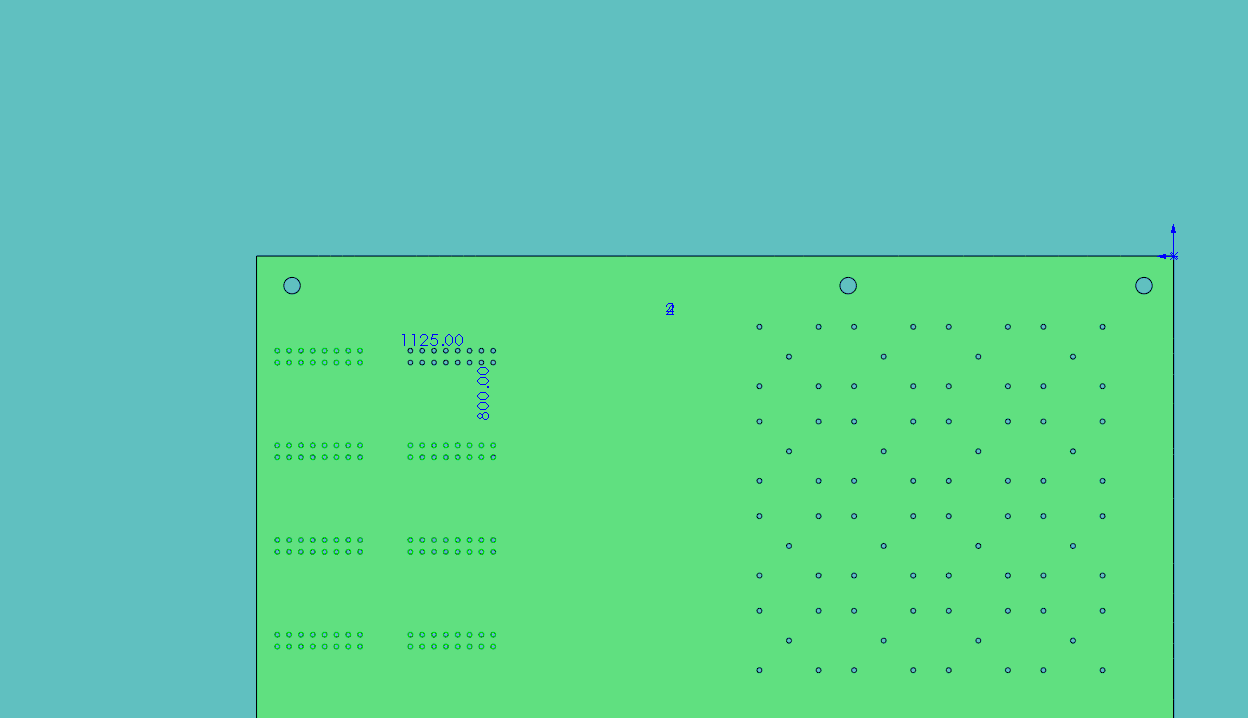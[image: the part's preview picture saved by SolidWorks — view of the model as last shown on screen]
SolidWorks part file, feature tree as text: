
SOLIDWORKS PART (.sldprt)
format: sldprt  version: not decoded by parser v0  size: 470,016 bytes
history: native  units: mm
features: sketch x4, cut_extrude x3, pattern_linear x2, material x1, extrude x1 (+13 scaffold rows collapsed)
feature tree (24):
  scaffold x13  (default folders/planes/origin — collapsed)
  material  "Material <not specified>"
  sketch  "Sketch1"  dims[D1=196.85mm D2=114.3mm]
  extrude  "PCB outline"  Depth=1.5748mm
  sketch  "mounting holes"  dims[c1.D1=3.556mm c1.D4=3.556mm c1.D7=3.556mm c1.D8=3.556mm c2.D4=3.556mm c2.D5=3.556mm c2.D6=3.556mm c2.D7=3.556mm c2.D8=3.556mm c2.D12=3.556mm c2.D13=3.556mm c2.D2=6.35mm c2.D3=6.35mm c3.D5=6.35mm c3.D6=6.35mm c3.D9=83.82mm c3.D10=~189.648312mm c3.D11=~7.201688mm c4.D10=6.35mm c4.D11=190.5mm c4.D9=96.52mm c5.D10=63.5mm c5.D11=119.38mm c5.D14=25.4mm]
  cut_extrude  "mounting holes cut"  Depth=2.54mm
  sketch  "Sketch2"  dims[c1.D1=1.0668mm c1.D2=1.0668mm c1.D3=1.0668mm c1.D4=1.0668mm c1.D5=1.0668mm c1.D6=6.35mm c1.D7=12.75mm c1.D8=12.7mm c1.D9=6.35mm c1.D10=21.59mm c1.D11=21.59mm c2.D10=15.24mm c2.D11=15.24mm]
  cut_extrude  "Cut-Extrude1"  Depth=1.5748mm
  pattern_linear  "LPattern1"  Count1=4 Count2=4 Spacing1=20.32mm Spacing2=20.32mm
  sketch  "Sketch3"  dims[c1.D1=1.016mm c1.D4=1.0668mm c1.D2=90.0deg c1.D3=1.27mm c2.D4=63.5mm c2.D5=2.54mm]
  cut_extrude  "DIO seed"  Depth=1.5748mm
  pattern_linear  "DIO pattern"  Count1=2 Count2=4 Spacing1=28.575mm Spacing2=20.32mm
decode coverage: 10 of 10 modeling features carry decoded parameters
note: ~ marks probable driven/reference dimensions
note: suppression state not decoded; provenance and decode notes live in map.json
